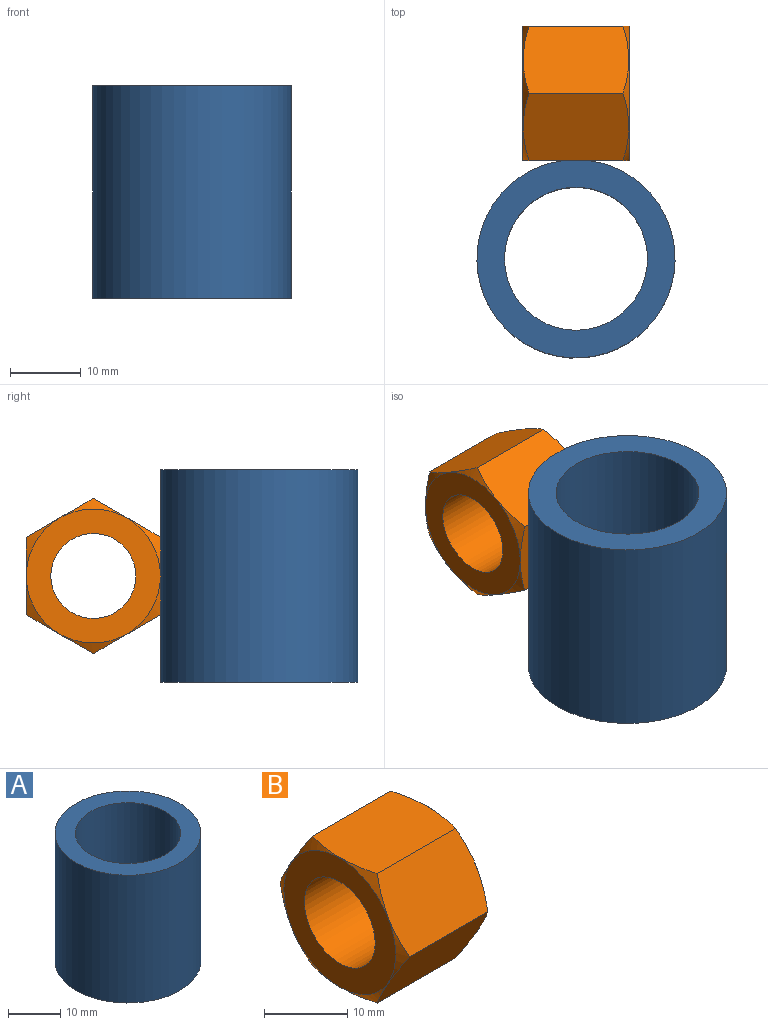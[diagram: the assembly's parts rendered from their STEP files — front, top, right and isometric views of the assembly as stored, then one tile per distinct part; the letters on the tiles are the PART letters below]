
ASSEMBLY  parts=2 mates=1
PART A: 5 faces, bbox 28x27.9x30 mm
  f0: cylinder r=10.1mm len=30mm, axis (0,0,-1), area 1903.8mm2, adj f2,f3
  f1: cylinder r=14mm len=30mm, axis (0,0,-1), area 2538.5mm2, adj f2,f3,f4
  f2: plane 28x27.9mm, normal (0,0,1), area 295.1mm2, adj f0,f1,f4
  f3: plane 28x27.9mm, normal (0,0,-1), area 295.1mm2, adj f0,f1,f4
  f4: plane 30x3.34mm, normal (0,1,0), area 100.2mm2, adj f1,f2,f3
PART B: 11 faces, bbox 15x21.9x21.9 mm
  f0: plane 18.94x18.94mm, normal (1,0,0), area 168.6mm2, adj f1,f4
  f1: cylinder r=6mm len=15mm, axis (-1,0,0), area 565.5mm2, adj f0,f2
  f2: plane 18.94x18.94mm, normal (-1,0,0), area 168.6mm2, adj f1,f3
  f3: cone r=9.47mm half-angle=60deg, axis (1,0,0), area 35.7mm2, adj f2,f5,f6,f7,f8,f9,f10
  f4: cone r=9.47mm half-angle=60deg, axis (-1,0,0), area 35.7mm2, adj f0,f5,f6,f7,f8,f9,f10
  f5: plane 14.97x9.5mm, normal (0,-0.87,-0.5), area 157.8mm2, adj f3,f4,f6,f10
  f6: plane 14.97x9.5mm, normal (0,-0.87,0.5), area 157.8mm2, adj f3,f4,f5,f7
  f7: plane 14.97x10.98mm, normal (0,0,1), area 157.8mm2, adj f3,f4,f6,f8
  f8: plane 14.97x9.5mm, normal (0,0.87,0.5), area 157.8mm2, adj f3,f4,f7,f9
  f9: plane 14.97x9.5mm, normal (0,0.87,-0.5), area 157.8mm2, adj f3,f4,f8,f10
  f10: plane 14.97x10.98mm, normal (0,0,-1), area 157.8mm2, adj f3,f4,f5,f9
PLACE A at identity
PLACE B rot(axis=(-1,0,0),90deg) t=(-7.5,23.4,15)mm
MATE fastened B.f10 <-> A.f4  axis (0,-1,0) through (0,13.9,15)mm
